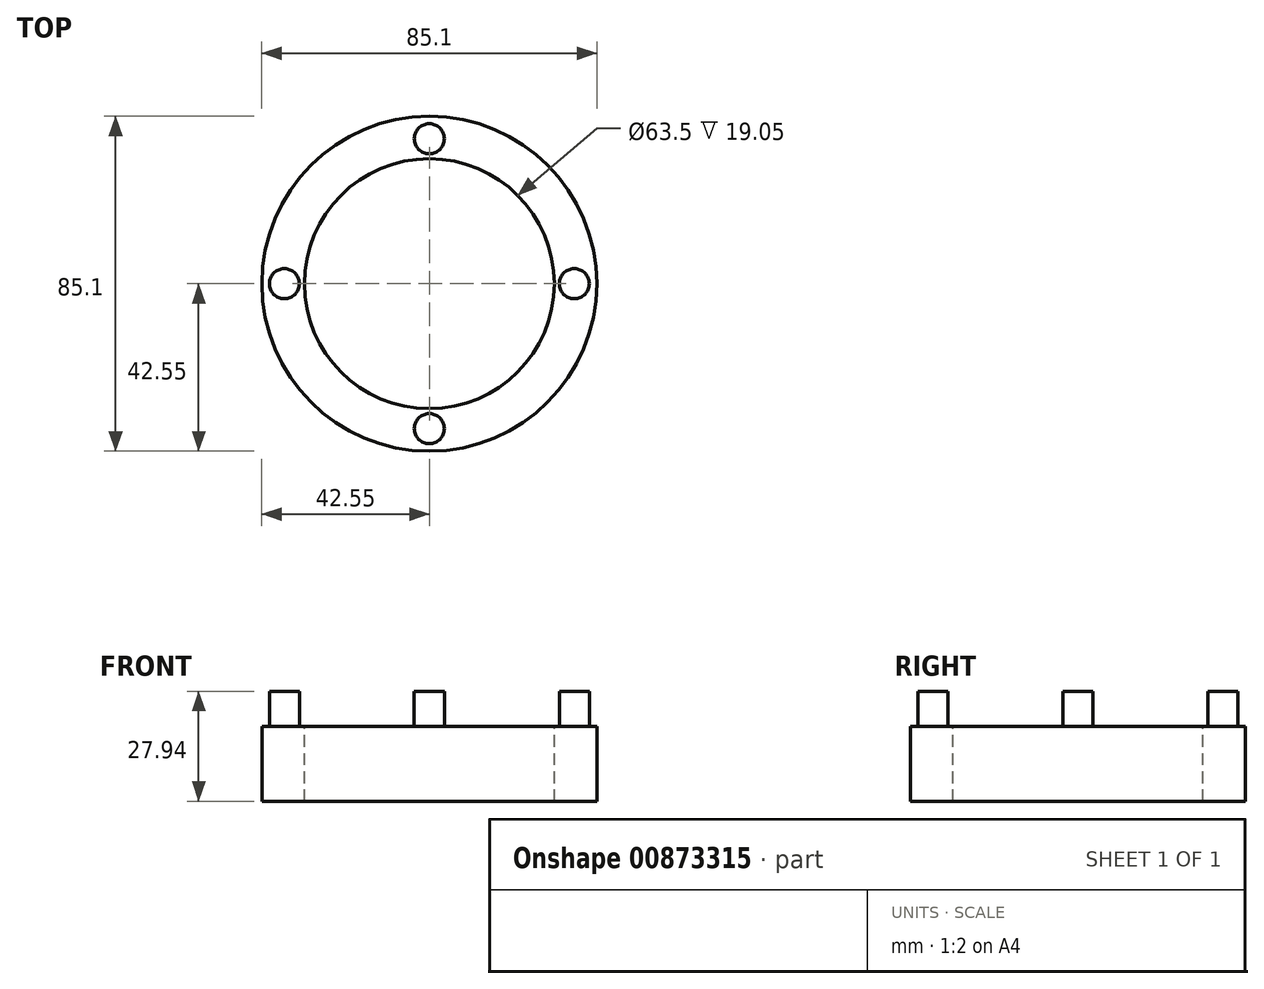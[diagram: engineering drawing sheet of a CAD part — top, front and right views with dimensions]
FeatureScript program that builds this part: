
annotation { "Feature Type Name" : "Feature", "Feature Type Description" : "" }
export const myFeature = defineFeature(function(context is Context, id is Id, definition is map)
    precondition{}
    {
        {
            var Q0;
            Q0=qCreatedBy(makeId("Top.planeOp"),FACE);
            var sketch = newSketch(context, id + "F0", { "sketchPlane" : qUnion([Q0])});
            skCircle(sketch, "E0", {"center": v(0, 0) * mm, "radius": 40.64 * mm});
            skCircle(sketch, "E1", {"center": v(0, 0) * mm, "radius": 36.83 * mm});
            skCircle(sketch, "E2", {"center": v(0, 36.83) * mm, "radius": 3.81 * mm});
            skCircle(sketch, "E3", {"center": v(36.83, 0) * mm, "radius": 3.81 * mm});
            skCircle(sketch, "E4", {"center": v(0, -36.83) * mm, "radius": 3.81 * mm});
            skCircle(sketch, "E5", {"center": v(-36.83, 0) * mm, "radius": 3.81 * mm});
            skCircle(sketch, "E6", {"center": v(0, 0) * mm, "radius": 31.75 * mm});
            skCircle(sketch, "E7", {"center": v(0, 0) * mm, "radius": 42.55 * mm});
            skSolve(sketch);
        }
        {
            var Q0;
            {var subQ0=sQuery(id+"F0.wireOp",EDGE,"E2");var subQ1=sQuery(id+"F0.wireOp",EDGE,"E1");var subQ2=makeQuery(id+"F0.imprint","INTERSECT",VERTEX,{"disambiguationData":[OD(0.0)],"derivedFrom":[subQ1,subQ0]});Q0=makeQuery(id+"F0.imprint","IMPRINT",FACE,{"disambiguationData":[TD([[makeQuery(id+"F0.imprint","IMPRINT",EDGE,{"disambiguationData":[TD([[subQ2,-1.0]])],"derivedFrom":subQ1}),-1.0]])]});}
            var Q1;
            {var subQ0=sQuery(id+"F0.wireOp",EDGE,"E2");var subQ1=sQuery(id+"F0.wireOp",EDGE,"E1");var subQ2=makeQuery(id+"F0.imprint","INTERSECT",VERTEX,{"disambiguationData":[OD(0.0)],"derivedFrom":[subQ1,subQ0]});Q1=makeQuery(id+"F0.imprint","IMPRINT",FACE,{"disambiguationData":[TD([[makeQuery(id+"F0.imprint","IMPRINT",EDGE,{"disambiguationData":[TD([[subQ2,-1.0]])],"derivedFrom":subQ1}),1.0]])]});}
            var Q2;
            {var subQ0=sQuery(id+"F0.wireOp",EDGE,"E5");var subQ1=sQuery(id+"F0.wireOp",EDGE,"E1");var subQ2=makeQuery(id+"F0.imprint","INTERSECT",VERTEX,{"disambiguationData":[OD(0.0)],"derivedFrom":[subQ1,subQ0]});Q2=makeQuery(id+"F0.imprint","IMPRINT",FACE,{"disambiguationData":[TD([[makeQuery(id+"F0.imprint","IMPRINT",EDGE,{"disambiguationData":[TD([[subQ2,-1.0]])],"derivedFrom":subQ1}),1.0]])]});}
            var Q3;
            {var subQ0=sQuery(id+"F0.wireOp",EDGE,"E5");var subQ1=sQuery(id+"F0.wireOp",EDGE,"E1");var subQ2=makeQuery(id+"F0.imprint","INTERSECT",VERTEX,{"disambiguationData":[OD(0.0)],"derivedFrom":[subQ1,subQ0]});Q3=makeQuery(id+"F0.imprint","IMPRINT",FACE,{"disambiguationData":[TD([[makeQuery(id+"F0.imprint","IMPRINT",EDGE,{"disambiguationData":[TD([[subQ2,-1.0]])],"derivedFrom":subQ1}),-1.0]])]});}
            var Q4;
            {var subQ0=sQuery(id+"F0.wireOp",EDGE,"E3");var subQ1=sQuery(id+"F0.wireOp",EDGE,"E1");var subQ2=makeQuery(id+"F0.imprint","INTERSECT",VERTEX,{"disambiguationData":[OD(0.0)],"derivedFrom":[subQ1,subQ0]});Q4=makeQuery(id+"F0.imprint","IMPRINT",FACE,{"disambiguationData":[TD([[makeQuery(id+"F0.imprint","IMPRINT",EDGE,{"disambiguationData":[TD([[subQ2,1.0]])],"derivedFrom":subQ1}),1.0]])]});}
            var Q5;
            {var subQ0=sQuery(id+"F0.wireOp",EDGE,"E3");var subQ1=sQuery(id+"F0.wireOp",EDGE,"E1");var subQ2=makeQuery(id+"F0.imprint","INTERSECT",VERTEX,{"disambiguationData":[OD(0.0)],"derivedFrom":[subQ1,subQ0]});Q5=makeQuery(id+"F0.imprint","IMPRINT",FACE,{"disambiguationData":[TD([[makeQuery(id+"F0.imprint","IMPRINT",EDGE,{"disambiguationData":[TD([[subQ2,1.0]])],"derivedFrom":subQ1}),-1.0]])]});}
            var Q6;
            {var subQ0=sQuery(id+"F0.wireOp",EDGE,"E4");var subQ1=sQuery(id+"F0.wireOp",EDGE,"E1");var subQ2=makeQuery(id+"F0.imprint","INTERSECT",VERTEX,{"disambiguationData":[OD(0.0)],"derivedFrom":[subQ1,subQ0]});Q6=makeQuery(id+"F0.imprint","IMPRINT",FACE,{"disambiguationData":[TD([[makeQuery(id+"F0.imprint","IMPRINT",EDGE,{"disambiguationData":[TD([[subQ2,-1.0]])],"derivedFrom":subQ1}),1.0]])]});}
            var Q7;
            {var subQ0=sQuery(id+"F0.wireOp",EDGE,"E4");var subQ1=sQuery(id+"F0.wireOp",EDGE,"E1");var subQ2=makeQuery(id+"F0.imprint","INTERSECT",VERTEX,{"disambiguationData":[OD(0.0)],"derivedFrom":[subQ1,subQ0]});Q7=makeQuery(id+"F0.imprint","IMPRINT",FACE,{"disambiguationData":[TD([[makeQuery(id+"F0.imprint","IMPRINT",EDGE,{"disambiguationData":[TD([[subQ2,-1.0]])],"derivedFrom":subQ1}),-1.0]])]});}
            extrude(context, id + "F1", {"entities" : qUnion([Q0, Q1, Q2, Q3, Q4, Q5, Q6, Q7]), "depth" : 8.9 * mm, "offsetDistance" : 25.4 * mm});
        }
        {
            var Q0;
            {var subQ0=sQuery(id+"F0.wireOp",EDGE,"E2");var subQ1=sQuery(id+"F0.wireOp",EDGE,"E1");var subQ2=makeQuery(id+"F0.imprint","INTERSECT",VERTEX,{"disambiguationData":[OD(1.0)],"derivedFrom":[subQ1,subQ0]});Q0=makeQuery(id+"F0.imprint","IMPRINT",FACE,{"disambiguationData":[TD([[makeQuery(id+"F0.imprint","IMPRINT",EDGE,{"disambiguationData":[TD([[subQ2,-1.0]])],"derivedFrom":subQ1}),1.0]])]});}
            var Q1;
            {var subQ0=sQuery(id+"F0.wireOp",EDGE,"E5");var subQ1=sQuery(id+"F0.wireOp",EDGE,"E0");var subQ2=makeQuery(id+"F0.imprint","INTERSECT",VERTEX,{"derivedFrom":[subQ1,subQ0]});Q1=makeQuery(id+"F0.imprint","IMPRINT",FACE,{"disambiguationData":[TD([[makeQuery(id+"F0.imprint","IMPRINT",EDGE,{"disambiguationData":[TD([[subQ2,-1.0]])],"derivedFrom":subQ1}),1.0]])]});}
            var Q2;
            {var subQ0=sQuery(id+"F0.wireOp",EDGE,"E5");var subQ1=sQuery(id+"F0.wireOp",EDGE,"E1");var subQ2=makeQuery(id+"F0.imprint","INTERSECT",VERTEX,{"disambiguationData":[OD(1.0)],"derivedFrom":[subQ1,subQ0]});Q2=makeQuery(id+"F0.imprint","IMPRINT",FACE,{"disambiguationData":[TD([[makeQuery(id+"F0.imprint","IMPRINT",EDGE,{"disambiguationData":[TD([[subQ2,-1.0]])],"derivedFrom":subQ1}),1.0]])]});}
            var Q3;
            {var subQ0=sQuery(id+"F0.wireOp",EDGE,"E2");var subQ1=sQuery(id+"F0.wireOp",EDGE,"E0");var subQ2=makeQuery(id+"F0.imprint","INTERSECT",VERTEX,{"derivedFrom":[subQ1,subQ0]});Q3=makeQuery(id+"F0.imprint","IMPRINT",FACE,{"disambiguationData":[TD([[makeQuery(id+"F0.imprint","IMPRINT",EDGE,{"disambiguationData":[TD([[subQ2,-1.0]])],"derivedFrom":subQ1}),1.0]])]});}
            var Q4;
            {var subQ0=sQuery(id+"F0.wireOp",EDGE,"E2");var subQ1=sQuery(id+"F0.wireOp",EDGE,"E0");var subQ2=makeQuery(id+"F0.imprint","INTERSECT",VERTEX,{"derivedFrom":[subQ1,subQ0]});Q4=makeQuery(id+"F0.imprint","IMPRINT",FACE,{"disambiguationData":[TD([[makeQuery(id+"F0.imprint","IMPRINT",EDGE,{"disambiguationData":[TD([[subQ2,1.0]])],"derivedFrom":subQ1}),1.0]])]});}
            var Q5;
            {var subQ0=sQuery(id+"F0.wireOp",EDGE,"E2");var subQ1=sQuery(id+"F0.wireOp",EDGE,"E1");var subQ2=makeQuery(id+"F0.imprint","INTERSECT",VERTEX,{"disambiguationData":[OD(0.0)],"derivedFrom":[subQ1,subQ0]});Q5=makeQuery(id+"F0.imprint","IMPRINT",FACE,{"disambiguationData":[TD([[makeQuery(id+"F0.imprint","IMPRINT",EDGE,{"disambiguationData":[TD([[subQ2,1.0]])],"derivedFrom":subQ1}),1.0]])]});}
            var Q6;
            {var subQ0=sQuery(id+"F0.wireOp",EDGE,"E3");var subQ1=sQuery(id+"F0.wireOp",EDGE,"E0");var subQ2=makeQuery(id+"F0.imprint","INTERSECT",VERTEX,{"derivedFrom":[subQ1,subQ0]});Q6=makeQuery(id+"F0.imprint","IMPRINT",FACE,{"disambiguationData":[TD([[makeQuery(id+"F0.imprint","IMPRINT",EDGE,{"disambiguationData":[TD([[subQ2,1.0]])],"derivedFrom":subQ1}),1.0]])]});}
            var Q7;
            {var subQ0=sQuery(id+"F0.wireOp",EDGE,"E4");var subQ1=sQuery(id+"F0.wireOp",EDGE,"E1");var subQ2=makeQuery(id+"F0.imprint","INTERSECT",VERTEX,{"disambiguationData":[OD(1.0)],"derivedFrom":[subQ1,subQ0]});Q7=makeQuery(id+"F0.imprint","IMPRINT",FACE,{"disambiguationData":[TD([[makeQuery(id+"F0.imprint","IMPRINT",EDGE,{"disambiguationData":[TD([[subQ2,-1.0]])],"derivedFrom":subQ1}),1.0]])]});}
            var Q8;
            {var subQ0=sQuery(id+"F0.wireOp",EDGE,"E2");var subQ1=sQuery(id+"F0.wireOp",EDGE,"E1");var subQ2=makeQuery(id+"F0.imprint","INTERSECT",VERTEX,{"disambiguationData":[OD(0.0)],"derivedFrom":[subQ1,subQ0]});Q8=makeQuery(id+"F0.imprint","IMPRINT",FACE,{"disambiguationData":[TD([[makeQuery(id+"F0.imprint","IMPRINT",EDGE,{"disambiguationData":[TD([[subQ2,-1.0]])],"derivedFrom":subQ1}),-1.0]])]});}
            var Q9;
            {var subQ0=sQuery(id+"F0.wireOp",EDGE,"E2");var subQ1=sQuery(id+"F0.wireOp",EDGE,"E1");var subQ2=makeQuery(id+"F0.imprint","INTERSECT",VERTEX,{"disambiguationData":[OD(0.0)],"derivedFrom":[subQ1,subQ0]});Q9=makeQuery(id+"F0.imprint","IMPRINT",FACE,{"disambiguationData":[TD([[makeQuery(id+"F0.imprint","IMPRINT",EDGE,{"disambiguationData":[TD([[subQ2,-1.0]])],"derivedFrom":subQ1}),1.0]])]});}
            var Q10;
            {var subQ0=sQuery(id+"F0.wireOp",EDGE,"E3");var subQ1=sQuery(id+"F0.wireOp",EDGE,"E1");var subQ2=makeQuery(id+"F0.imprint","INTERSECT",VERTEX,{"disambiguationData":[OD(0.0)],"derivedFrom":[subQ1,subQ0]});Q10=makeQuery(id+"F0.imprint","IMPRINT",FACE,{"disambiguationData":[TD([[makeQuery(id+"F0.imprint","IMPRINT",EDGE,{"disambiguationData":[TD([[subQ2,1.0]])],"derivedFrom":subQ1}),1.0]])]});}
            var Q11;
            {var subQ0=sQuery(id+"F0.wireOp",EDGE,"E3");var subQ1=sQuery(id+"F0.wireOp",EDGE,"E1");var subQ2=makeQuery(id+"F0.imprint","INTERSECT",VERTEX,{"disambiguationData":[OD(0.0)],"derivedFrom":[subQ1,subQ0]});Q11=makeQuery(id+"F0.imprint","IMPRINT",FACE,{"disambiguationData":[TD([[makeQuery(id+"F0.imprint","IMPRINT",EDGE,{"disambiguationData":[TD([[subQ2,1.0]])],"derivedFrom":subQ1}),-1.0]])]});}
            var Q12;
            {var subQ0=sQuery(id+"F0.wireOp",EDGE,"E5");var subQ1=sQuery(id+"F0.wireOp",EDGE,"E1");var subQ2=makeQuery(id+"F0.imprint","INTERSECT",VERTEX,{"disambiguationData":[OD(0.0)],"derivedFrom":[subQ1,subQ0]});Q12=makeQuery(id+"F0.imprint","IMPRINT",FACE,{"disambiguationData":[TD([[makeQuery(id+"F0.imprint","IMPRINT",EDGE,{"disambiguationData":[TD([[subQ2,-1.0]])],"derivedFrom":subQ1}),-1.0]])]});}
            var Q13;
            {var subQ0=sQuery(id+"F0.wireOp",EDGE,"E5");var subQ1=sQuery(id+"F0.wireOp",EDGE,"E1");var subQ2=makeQuery(id+"F0.imprint","INTERSECT",VERTEX,{"disambiguationData":[OD(0.0)],"derivedFrom":[subQ1,subQ0]});Q13=makeQuery(id+"F0.imprint","IMPRINT",FACE,{"disambiguationData":[TD([[makeQuery(id+"F0.imprint","IMPRINT",EDGE,{"disambiguationData":[TD([[subQ2,-1.0]])],"derivedFrom":subQ1}),1.0]])]});}
            var Q14;
            {var subQ0=sQuery(id+"F0.wireOp",EDGE,"E4");var subQ1=sQuery(id+"F0.wireOp",EDGE,"E1");var subQ2=makeQuery(id+"F0.imprint","INTERSECT",VERTEX,{"disambiguationData":[OD(0.0)],"derivedFrom":[subQ1,subQ0]});Q14=makeQuery(id+"F0.imprint","IMPRINT",FACE,{"disambiguationData":[TD([[makeQuery(id+"F0.imprint","IMPRINT",EDGE,{"disambiguationData":[TD([[subQ2,-1.0]])],"derivedFrom":subQ1}),1.0]])]});}
            var Q15;
            {var subQ0=sQuery(id+"F0.wireOp",EDGE,"E4");var subQ1=sQuery(id+"F0.wireOp",EDGE,"E1");var subQ2=makeQuery(id+"F0.imprint","INTERSECT",VERTEX,{"disambiguationData":[OD(0.0)],"derivedFrom":[subQ1,subQ0]});Q15=makeQuery(id+"F0.imprint","IMPRINT",FACE,{"disambiguationData":[TD([[makeQuery(id+"F0.imprint","IMPRINT",EDGE,{"disambiguationData":[TD([[subQ2,-1.0]])],"derivedFrom":subQ1}),-1.0]])]});}
            var Q16;
            Q16=makeQuery(id+"F0.imprint","IMPRINT",FACE,{"disambiguationData":[TD([[makeQuery(id+"F0.imprint","IMPRINT",EDGE,{"derivedFrom":sQuery(id+"F0.wireOp",EDGE,"E7")}),1.0]])]});
            extrude(context, id + "F2", {"entities" : qUnion([Q0, Q1, Q2, Q3, Q4, Q5, Q6, Q7, Q8, Q9, Q10, Q11, Q12, Q13, Q14, Q15, Q16]), "depth" : -19.05 * mm, "offsetDistance" : 25.4 * mm});
        }
    });
